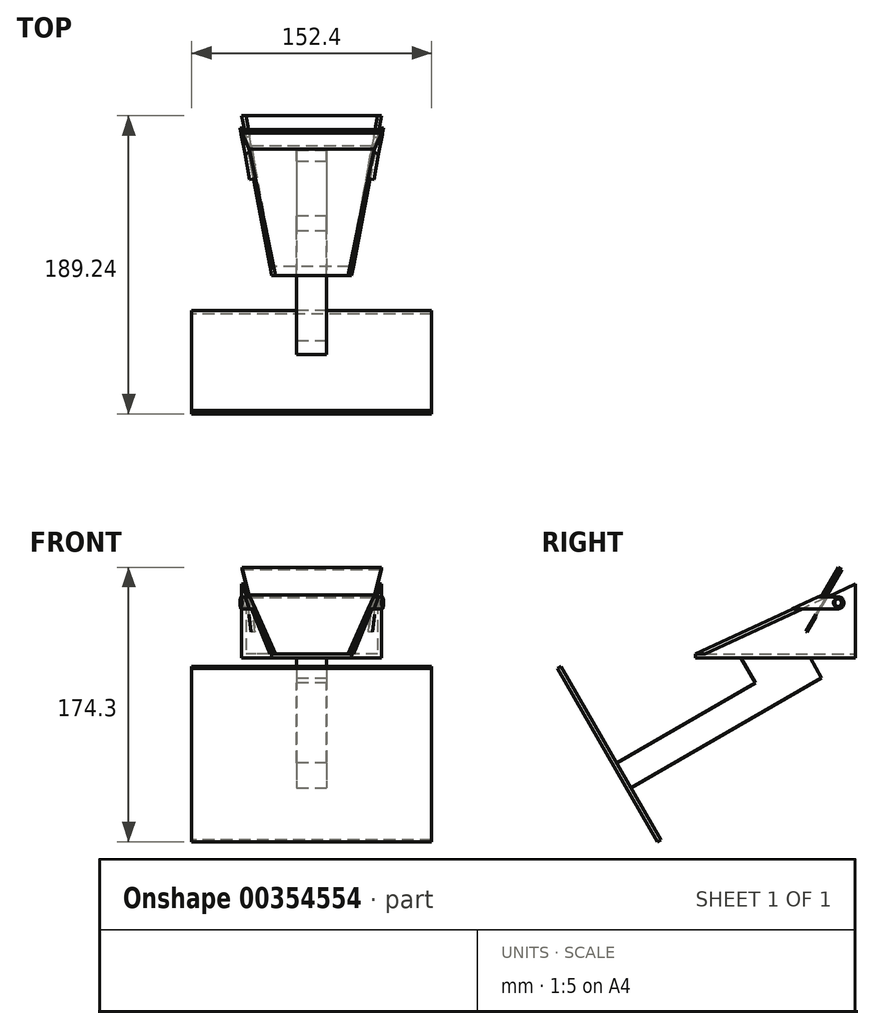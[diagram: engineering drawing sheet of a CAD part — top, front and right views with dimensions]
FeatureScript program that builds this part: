
annotation { "Feature Type Name" : "Feature", "Feature Type Description" : "" }
export const myFeature = defineFeature(function(context is Context, id is Id, definition is map)
    precondition{}
    {
        {
            var Q0;
            Q0=qCreatedBy(makeId("Top.planeOp"),FACE);
            var sketch = newSketch(context, id + "F0", { "sketchPlane" : qUnion([Q0])});
            skPoint(sketch, "E0.middle", {"position": v(0, 0) * mm});
            skLineSegment(sketch, "E1", {"start": v(-44.45, 50.8) * mm, "end": v(-25.4, -50.8) * mm});
            skLineSegment(sketch, "E2", {"start": v(-25.4, -50.8) * mm, "end": v(25.4, -50.8) * mm});
            skLineSegment(sketch, "E3", {"start": v(25.4, -50.8) * mm, "end": v(44.45, 50.8) * mm});
            skLineSegment(sketch, "E4", {"start": v(44.45, 50.8) * mm, "end": v(-44.45, 50.8) * mm});
            skLineSegment(sketch, "E5", {"start": v(0, 50.8) * mm, "end": v(0, -50.8) * mm, "construction": true});
            skLineSegment(sketch, "E6", {"start": v(-41.87, 50.8) * mm, "end": v(-22.82, -50.8) * mm});
            skLineSegment(sketch, "E7", {"start": v(22.82, -50.8) * mm, "end": v(41.87, 50.8) * mm});
            skSolve(sketch);
        }
        {
            var Q0;
            Q0=makeQuery(id+"F0.imprint","IMPRINT",FACE,{"disambiguationData":[TD([[makeQuery(id+"F0.imprint","IMPRINT",EDGE,{"derivedFrom":sQuery(id+"F0.wireOp",EDGE,"E1")}),1.0]])]});
            var Q1;
            {var subQ0=sQuery(id+"F0.wireOp",EDGE,"E3");Q1=makeQuery(id+"F0.imprint","IMPRINT",FACE,{"disambiguationData":[TD([[makeQuery(id+"F0.imprint","IMPRINT",EDGE,{"derivedFrom":subQ0}),1.0]])]});}
            var Q2;
            {var subQ0=sQuery(id+"F0.wireOp",EDGE,"E6");Q2=makeQuery(id+"F0.imprint","IMPRINT",FACE,{"disambiguationData":[TD([[makeQuery(id+"F0.imprint","IMPRINT",EDGE,{"derivedFrom":subQ0}),1.0]])]});}
            extrude(context, id + "F1", {"entities" : qUnion([Q0, Q1, Q2]), "depth" : 2.54 * mm});
        }
        {
            var Q0;
            Q0=makeQuery(id+"F1.opExtrude","CAP_EDGE",EDGE,{"disambiguationData":[OSD([sQuery(id+"F0.wireOp",EDGE,"E2")])],"isStart":false});
            cPlane(context, id + "F2", {"entities" : qUnion([Q0]), "cplaneType" : CPlaneType.LINE_ANGLE, "offset" : 25.4 * mm, "angle" : 65 * degree, "oppositeDirection" : true, "width" : 152.4 * mm, "height" : 152.4 * mm});
        }
        {
            var Q0;
            Q0=qCreatedBy(id+"F2.planeOp",FACE);
            var sketch = newSketch(context, id + "F3", { "sketchPlane" : qUnion([Q0])});
            skLineSegment(sketch, "E8", {"start": v(-23.04, 44.97) * mm, "end": v(-39.7, -43.93) * mm});
            skLineSegment(sketch, "E9", {"start": v(-39.7, -43.93) * mm, "end": v(39.7, -43.93) * mm});
            skLineSegment(sketch, "E10", {"start": v(39.7, -43.93) * mm, "end": v(23.04, 44.97) * mm});
            skLineSegment(sketch, "E11", {"start": v(23.04, 44.97) * mm, "end": v(-23.04, 44.97) * mm});
            skSolve(sketch);
        }
        {
            var Q0;
            Q0=makeQuery(id+"F3.imprint","IMPRINT",FACE,{"disambiguationData":[TD([[makeQuery(id+"F3.imprint","IMPRINT",EDGE,{"derivedFrom":sQuery(id+"F3.wireOp",EDGE,"E8")}),1.0]])]});
            extrude(context, id + "F4", {"entities" : qUnion([Q0]), "depth" : 2.54 * mm});
        }
        {
            var Q0;
            {var subQ0=sQuery(id+"F0.wireOp",EDGE,"E1");Q0=makeQuery(id+"F0.imprint","IMPRINT",FACE,{"disambiguationData":[TD([[makeQuery(id+"F0.imprint","IMPRINT",EDGE,{"derivedFrom":subQ0}),1.0]])]});}
            var Q1;
            {var subQ0=sQuery(id+"F0.wireOp",EDGE,"E3");Q1=makeQuery(id+"F0.imprint","IMPRINT",FACE,{"disambiguationData":[TD([[makeQuery(id+"F0.imprint","IMPRINT",EDGE,{"derivedFrom":subQ0}),1.0]])]});}
            var Q2;
            Q2=makeQuery(id+"F4.opExtrude","CAP_FACE",FACE,{"disambiguationData":[OSD([sQuery(id+"F3.wireOp",EDGE,"E8"),sQuery(id+"F3.wireOp",EDGE,"E9"),sQuery(id+"F3.wireOp",EDGE,"E10"),sQuery(id+"F3.wireOp",EDGE,"E11")])],"isStart":false});
            extrude(context, id + "F5", {"entities" : qUnion([Q0, Q1]), "operationType" : NewBodyOperationType.ADD, "endBound" : BoundingType.UP_TO_SURFACE, "endBoundEntityFace" : qUnion([Q2]), "depth" : 27.94 * mm});
        }
        {
            var Q0;
            {var subQ0=sQuery(id+"F0.wireOp",EDGE,"E1");Q0=makeQuery(id+"F5.boolean.opBoolean","MERGE",FACE,{"derivedFrom":[makeQuery(id+"F1.opExtrude","SWEPT_FACE",FACE,{"disambiguationData":[OSD([subQ0])]}),makeQuery(id+"F5.opExtrude","SWEPT_FACE",FACE,{"disambiguationData":[OSD([subQ0])]})]});}
            var sketch = newSketch(context, id + "F6", { "sketchPlane" : qUnion([Q0])});
            skLineSegment(sketch, "E12", {"start": v(-34.07, 38.96) * mm, "end": v(-46.77, 38.96) * mm});
            skLineSegment(sketch, "E13", {"start": v(-46.77, 31.34) * mm, "end": v(-17.38, 31.34) * mm});
            skArc(sketch, "E14", {"start": v(-46.77, 38.96) * mm, "mid": v(-50.58, 35.15) * mm, "end": v(-46.77, 31.34) * mm});
            skLineSegment(sketch, "E15", {"start": v(-17.38, 31.34) * mm, "end": v(-34.07, 38.96) * mm});
            skCircle(sketch, "E16", {"center": v(-46.77, 35.15) * mm, "radius": 2.54 * mm});
            skSolve(sketch);
        }
        {
            var Q0;
            {var subQ0=sQuery(id+"F6.wireOp",EDGE,"E15");Q0=makeQuery(id+"F6.imprint","IMPRINT",FACE,{"disambiguationData":[TD([[makeQuery(id+"F6.imprint","IMPRINT",EDGE,{"derivedFrom":subQ0}),1.0]])]});}
            var Q1;
            {var subQ0=sQuery(id+"F6.wireOp",EDGE,"E14");Q1=makeQuery(id+"F6.imprint","IMPRINT",FACE,{"disambiguationData":[TD([[makeQuery(id+"F6.imprint","IMPRINT",EDGE,{"derivedFrom":subQ0}),1.0]])]});}
            var Q2;
            Q2=makeQuery(id+"F4.opExtrude","SWEPT_FACE",FACE,{"disambiguationData":[OSD([sQuery(id+"F3.wireOp",EDGE,"E8")])]});
            extrude(context, id + "F7", {"entities" : qUnion([Q0, Q1]), "depth" : 2.54 * mm, "hasSecondDirection" : true, "secondDirectionBound" : SecondDirectionBoundingType.UP_TO_SURFACE, "secondDirectionOppositeDirection" : true, "secondDirectionBoundEntityFace" : qUnion([Q2]), "secondDirectionDepth" : 25.4 * mm});
        }
        {
            var Q0;
            Q0=makeQuery(id+"F6.imprint","IMPRINT",FACE,{"disambiguationData":[TD([[makeQuery(id+"F6.imprint","IMPRINT",EDGE,{"derivedFrom":sQuery(id+"F6.wireOp",EDGE,"E16")}),1.0]])]});
            extrude(context, id + "F8", {"entities" : qUnion([Q0]), "oppositeDirection" : true, "depth" : 7.62 * mm});
        }
        {
            var Q0;
            Q0=makeQuery(id+"F7.opExtrude","SWEPT_BODY",BODY,{"disambiguationData":[OSD([sQuery(id+"F6.wireOp",EDGE,"E12"),sQuery(id+"F6.wireOp",EDGE,"E13"),sQuery(id+"F6.wireOp",EDGE,"E14"),sQuery(id+"F6.wireOp",EDGE,"E15"),sQuery(id+"F6.wireOp",EDGE,"E16")])]});
            var Q1;
            Q1=makeQuery(id+"F8.opExtrude","SWEPT_BODY",BODY,{"disambiguationData":[OSD([sQuery(id+"F6.wireOp",EDGE,"E16")])]});
            var Q2;
            Q2=qCreatedBy(makeId("Right.planeOp"),FACE);
            mirror(context, id + "F9", {"entities" : qUnion([Q0, Q1]), "mirrorPlane" : qUnion([Q2])});
        }
        {
            var Q0;
            Q0=makeQuery(id+"F1.opExtrude","SWEPT_BODY",BODY,{"disambiguationData":[OSD([sQuery(id+"F0.wireOp",EDGE,"E1"),sQuery(id+"F0.wireOp",EDGE,"E2"),sQuery(id+"F0.wireOp",EDGE,"E3"),sQuery(id+"F0.wireOp",EDGE,"E4")])]});
            var Q1;
            Q1=makeQuery(id+"F9.opPattern","COPY",BODY,{"derivedFrom":makeQuery(id+"F7.opExtrude","SWEPT_BODY",BODY,{"disambiguationData":[OSD([sQuery(id+"F6.wireOp",EDGE,"E12"),sQuery(id+"F6.wireOp",EDGE,"E13"),sQuery(id+"F6.wireOp",EDGE,"E14"),sQuery(id+"F6.wireOp",EDGE,"E15"),sQuery(id+"F6.wireOp",EDGE,"E16")])]}),"instanceName":"1"});
            var Q2;
            Q2=makeQuery(id+"F7.opExtrude","SWEPT_BODY",BODY,{"disambiguationData":[OSD([sQuery(id+"F6.wireOp",EDGE,"E12"),sQuery(id+"F6.wireOp",EDGE,"E13"),sQuery(id+"F6.wireOp",EDGE,"E14"),sQuery(id+"F6.wireOp",EDGE,"E15"),sQuery(id+"F6.wireOp",EDGE,"E16")])]});
            booleanBodies(context, id + "F10", {"operationType" : BooleanOperationType.SUBTRACTION, "tools" : qUnion([Q0]), "targets" : qUnion([Q1, Q2]), "keepTools" : true});
        }
        {
            var Q0;
            Q0=makeQuery(id+"F4.opExtrude","SWEPT_BODY",BODY,{"disambiguationData":[OSD([sQuery(id+"F3.wireOp",EDGE,"E8"),sQuery(id+"F3.wireOp",EDGE,"E9"),sQuery(id+"F3.wireOp",EDGE,"E10"),sQuery(id+"F3.wireOp",EDGE,"E11")])]});
            var Q1;
            Q1=makeQuery(id+"F9.opPattern","COPY",BODY,{"derivedFrom":makeQuery(id+"F7.opExtrude","SWEPT_BODY",BODY,{"disambiguationData":[OSD([sQuery(id+"F6.wireOp",EDGE,"E12"),sQuery(id+"F6.wireOp",EDGE,"E13"),sQuery(id+"F6.wireOp",EDGE,"E14"),sQuery(id+"F6.wireOp",EDGE,"E15"),sQuery(id+"F6.wireOp",EDGE,"E16")])]}),"instanceName":"1"});
            var Q2;
            Q2=makeQuery(id+"F7.opExtrude","SWEPT_BODY",BODY,{"disambiguationData":[OSD([sQuery(id+"F6.wireOp",EDGE,"E12"),sQuery(id+"F6.wireOp",EDGE,"E13"),sQuery(id+"F6.wireOp",EDGE,"E14"),sQuery(id+"F6.wireOp",EDGE,"E15"),sQuery(id+"F6.wireOp",EDGE,"E16")])]});
            booleanBodies(context, id + "F11", {"operationType" : BooleanOperationType.UNION, "tools" : qUnion([Q0, Q1, Q2])});
        }
        {
            var Q0;
            Q0=makeQuery(id+"F9.opPattern","COPY",BODY,{"derivedFrom":makeQuery(id+"F8.opExtrude","SWEPT_BODY",BODY,{"disambiguationData":[OSD([sQuery(id+"F6.wireOp",EDGE,"E16")])]}),"instanceName":"1"});
            var Q1;
            Q1=makeQuery(id+"F8.opExtrude","SWEPT_BODY",BODY,{"disambiguationData":[OSD([sQuery(id+"F6.wireOp",EDGE,"E16")])]});
            var Q2;
            Q2=makeQuery(id+"F1.opExtrude","SWEPT_BODY",BODY,{"disambiguationData":[OSD([sQuery(id+"F0.wireOp",EDGE,"E1"),sQuery(id+"F0.wireOp",EDGE,"E2"),sQuery(id+"F0.wireOp",EDGE,"E3"),sQuery(id+"F0.wireOp",EDGE,"E4")])]});
            booleanBodies(context, id + "F12", {"operationType" : BooleanOperationType.SUBTRACTION, "tools" : qUnion([Q0, Q1]), "targets" : qUnion([Q2])});
        }
        {
            var Q0;
            Q0=makeQuery(id+"F4.opExtrude","CAP_EDGE",EDGE,{"disambiguationData":[OSD([sQuery(id+"F3.wireOp",EDGE,"E9")])],"isStart":true});
            cPlane(context, id + "F13", {"entities" : qUnion([Q0]), "cplaneType" : CPlaneType.LINE_ANGLE, "offset" : 25.4 * mm, "angle" : 30 * degree, "oppositeDirection" : true, "width" : 152.4 * mm, "height" : 152.4 * mm});
        }
        {
            var Q0;
            Q0=qCreatedBy(id+"F13.planeOp",FACE);
            var sketch = newSketch(context, id + "F14", { "sketchPlane" : qUnion([Q0])});
            skLineSegment(sketch, "E17.bottom", {"start": v(39.7, 49.62) * mm, "end": v(-39.7, 49.62) * mm});
            skLineSegment(sketch, "E17.top", {"start": v(44.36, 69.94) * mm, "end": v(-44.36, 69.94) * mm});
            skLineSegment(sketch, "E17.left", {"start": v(39.7, 49.62) * mm, "end": v(44.36, 69.94) * mm});
            skLineSegment(sketch, "E17.right", {"start": v(-39.7, 49.62) * mm, "end": v(-44.36, 69.94) * mm});
            skSolve(sketch);
        }
        {
            var Q0;
            Q0=makeQuery(id+"F14.imprint","IMPRINT",FACE,{"disambiguationData":[TD([[makeQuery(id+"F14.imprint","IMPRINT",EDGE,{"derivedFrom":sQuery(id+"F14.wireOp",EDGE,"E17.bottom")}),-1.0]])]});
            extrude(context, id + "F15", {"entities" : qUnion([Q0]), "depth" : 2.54 * mm});
        }
        {
            var Q0;
            Q0=makeQuery(id+"F4.opExtrude","SWEPT_FACE",FACE,{"disambiguationData":[OSD([sQuery(id+"F3.wireOp",EDGE,"E9")])]});
            var Q1;
            Q1=makeQuery(id+"F15.opExtrude","SWEPT_FACE",FACE,{"disambiguationData":[OSD([sQuery(id+"F14.wireOp",EDGE,"E17.bottom")])]});
            extrude(context, id + "F16", {"entities" : qUnion([Q0]), "operationType" : NewBodyOperationType.ADD, "endBound" : BoundingType.UP_TO_SURFACE, "endBoundEntityFace" : qUnion([Q1]), "depth" : 25.4 * mm});
        }
        {
            var Q0;
            Q0=makeQuery(id+"F16.opExtrude","CAP_FACE",FACE,{"disambiguationData":[OSD([sQuery(id+"F3.wireOp",EDGE,"E9")])],"isStart":false});
            extrude(context, id + "F17", {"entities" : qUnion([Q0]), "operationType" : NewBodyOperationType.REMOVE, "oppositeDirection" : true, "depth" : 25.4 * mm});
        }
        {
            var Q0;
            Q0=makeQuery(id+"F1.opExtrude","CAP_EDGE",EDGE,{"disambiguationData":[OSD([sQuery(id+"F0.wireOp",EDGE,"E4")])],"isStart":true});
            cPlane(context, id + "F18", {"entities" : qUnion([Q0]), "cplaneType" : CPlaneType.LINE_ANGLE, "offset" : 25.4 * mm, "angle" : 60 * degree, "width" : 152.4 * mm, "height" : 152.4 * mm});
        }
        {
            var Q0;
            Q0=qCreatedBy(id+"F18.planeOp",FACE);
            var sketch = newSketch(context, id + "F19", { "sketchPlane" : qUnion([Q0])});
            skLineSegment(sketch, "E18.bottom", {"start": v(-9.52, 19.05) * mm, "end": v(9.53, 19.05) * mm});
            skLineSegment(sketch, "E18.top", {"start": v(-9.53, -19.05) * mm, "end": v(9.52, -19.05) * mm});
            skLineSegment(sketch, "E18.left", {"start": v(-9.52, 19.05) * mm, "end": v(-9.53, -19.05) * mm});
            skLineSegment(sketch, "E18.right", {"start": v(9.53, 19.05) * mm, "end": v(9.52, -19.05) * mm});
            skPoint(sketch, "E18.middle", {"position": v(0, 0) * mm});
            skSolve(sketch);
        }
        {
            var Q0;
            Q0=makeQuery(id+"F19.imprint","IMPRINT",FACE,{"disambiguationData":[TD([[makeQuery(id+"F19.imprint","IMPRINT",EDGE,{"derivedFrom":sQuery(id+"F19.wireOp",EDGE,"E18.bottom")}),-1.0]])]});
            var Q1;
            Q1=makeQuery(id+"F1.opExtrude","CAP_FACE",FACE,{"disambiguationData":[OSD([sQuery(id+"F0.wireOp",EDGE,"E1"),sQuery(id+"F0.wireOp",EDGE,"E2"),sQuery(id+"F0.wireOp",EDGE,"E3"),sQuery(id+"F0.wireOp",EDGE,"E4")])],"isStart":true});
            extrude(context, id + "F20", {"entities" : qUnion([Q0]), "operationType" : NewBodyOperationType.ADD, "endBound" : BoundingType.UP_TO_SURFACE, "endBoundEntityFace" : qUnion([Q1]), "depth" : 25.4 * mm});
        }
        {
            var Q0;
            Q0=makeQuery(id+"F20.opExtrude","SWEPT_FACE",FACE,{"disambiguationData":[OSD([sQuery(id+"F19.wireOp",EDGE,"E18.top")])]});
            var sketch = newSketch(context, id + "F21", { "sketchPlane" : qUnion([Q0])});
            skLineSegment(sketch, "E19.bottom", {"start": v(9.52, -25.4) * mm, "end": v(-9.53, -25.4) * mm});
            skLineSegment(sketch, "E19.top", {"start": v(9.52, -7.2) * mm, "end": v(-9.53, -7.2) * mm});
            skLineSegment(sketch, "E19.left", {"start": v(9.52, -25.4) * mm, "end": v(9.52, -7.2) * mm});
            skLineSegment(sketch, "E19.right", {"start": v(-9.53, -25.4) * mm, "end": v(-9.53, -7.2) * mm});
            skSolve(sketch);
        }
        {
            var Q0;
            Q0=makeQuery(id+"F21.imprint","IMPRINT",FACE,{"disambiguationData":[TD([[makeQuery(id+"F21.imprint","IMPRINT",EDGE,{"derivedFrom":sQuery(id+"F21.wireOp",EDGE,"E19.bottom")}),1.0]])]});
            extrude(context, id + "F22", {"entities" : qUnion([Q0]), "operationType" : NewBodyOperationType.ADD, "depth" : 101.6 * mm});
        }
        {
            var Q0;
            Q0=makeQuery(id+"F22.opExtrude","CAP_FACE",FACE,{"disambiguationData":[OSD([sQuery(id+"F21.wireOp",EDGE,"E19.bottom"),sQuery(id+"F21.wireOp",EDGE,"E19.top"),sQuery(id+"F21.wireOp",EDGE,"E19.left"),sQuery(id+"F21.wireOp",EDGE,"E19.right")])],"isStart":false});
            var sketch = newSketch(context, id + "F23", { "sketchPlane" : qUnion([Q0])});
            skLineSegment(sketch, "E20.bottom", {"start": v(76.2, -63.5) * mm, "end": v(-76.2, -63.5) * mm});
            skLineSegment(sketch, "E20.top", {"start": v(76.2, 63.5) * mm, "end": v(-76.2, 63.5) * mm});
            skLineSegment(sketch, "E20.left", {"start": v(76.2, -63.5) * mm, "end": v(76.2, 63.5) * mm});
            skLineSegment(sketch, "E20.right", {"start": v(-76.2, -63.5) * mm, "end": v(-76.2, 63.5) * mm});
            skPoint(sketch, "E20.middle", {"position": v(0, 0) * mm});
            skSolve(sketch);
        }
        {
            var Q0;
            Q0=makeQuery(id+"F23.imprint","IMPRINT",FACE,{"disambiguationData":[TD([[makeQuery(id+"F23.imprint","IMPRINT",EDGE,{"derivedFrom":sQuery(id+"F23.wireOp",EDGE,"E20.bottom")}),-1.0]])]});
            var Q1;
            Q1=makeQuery(id+"F23.imprint","IMPRINT",FACE,{"disambiguationData":[TD([[makeQuery(id+"F23.imprint","IMPRINT",EDGE,{"derivedFrom":makeQuery(id+"F22.opExtrude","CAP_EDGE",EDGE,{"disambiguationData":[OSD([sQuery(id+"F21.wireOp",EDGE,"E19.bottom")])],"isStart":false})}),1.0]])]});
            extrude(context, id + "F24", {"entities" : qUnion([Q0, Q1]), "operationType" : NewBodyOperationType.ADD, "depth" : 2.54 * mm});
        }
    });
